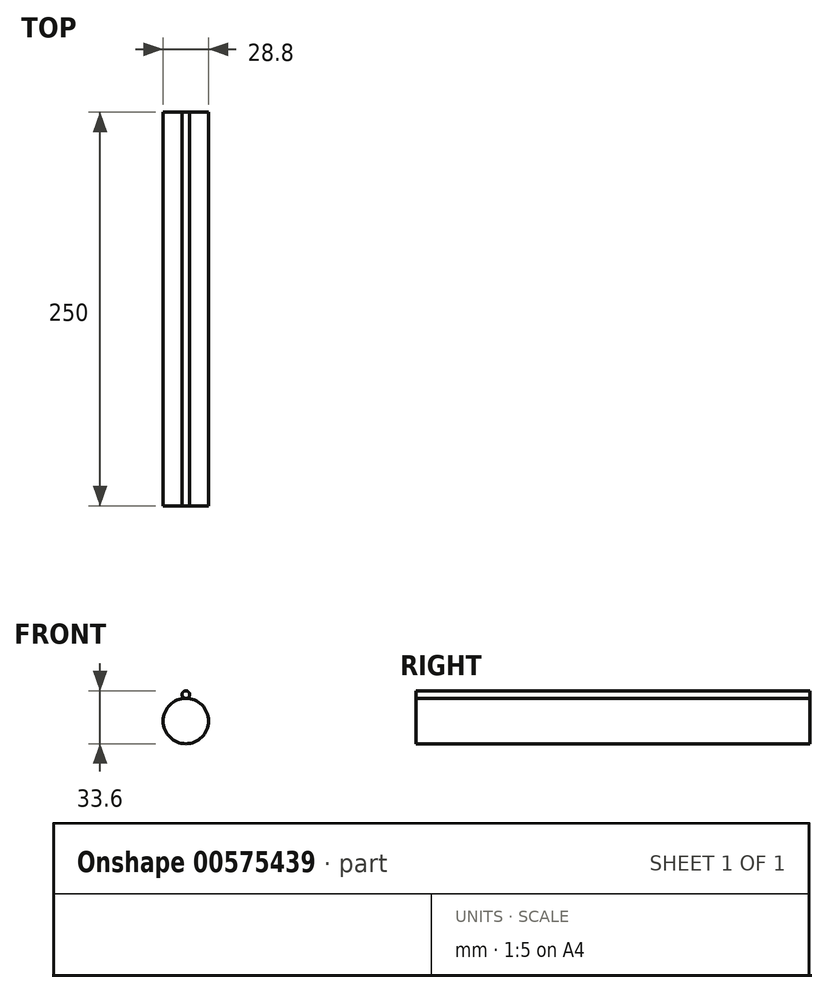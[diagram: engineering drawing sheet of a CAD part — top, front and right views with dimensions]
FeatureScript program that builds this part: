
annotation { "Feature Type Name" : "Feature", "Feature Type Description" : "" }
export const myFeature = defineFeature(function(context is Context, id is Id, definition is map)
    precondition{}
    {
        {
            var Q0;
            Q0=qCreatedBy(makeId("Front.planeOp"),FACE);
            var sketch = newSketch(context, id + "F0", { "sketchPlane" : qUnion([Q0])});
            skCircle(sketch, "E0", {"center": v(0, 0.32) * mm, "radius": 14.4 * mm});
            skCircle(sketch, "E1", {"center": v(0, 17.12) * mm, "radius": 2.4 * mm});
            skSolve(sketch);
        }
        {
            var Q0;
            Q0 = qSketchRegion(id + "F0", true);
            var Q1;
            Q1=makeQuery(id+"F0.imprint","IMPRINT",FACE,{"disambiguationData":[TD([[makeQuery(id+"F0.imprint","IMPRINT",EDGE,{"derivedFrom":sQuery(id+"F0.wireOp",EDGE,"E0")}),1.0]])]});
            extrude(context, id + "F1", {"entities" : qUnion([Q0, Q1]), "endBound" : BoundingType.SYMMETRIC, "depth" : 250 * mm, "offsetDistance" : 25 * mm});
        }
    });
